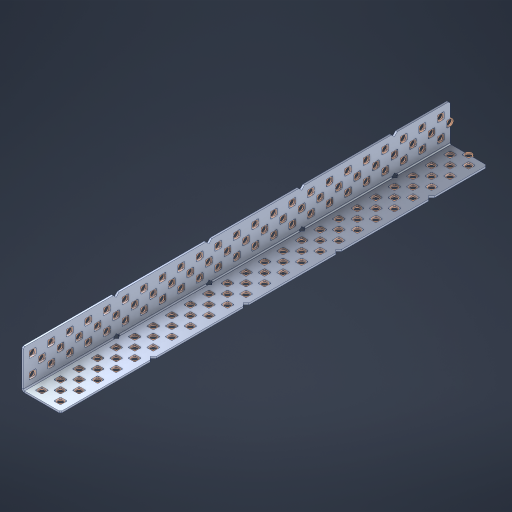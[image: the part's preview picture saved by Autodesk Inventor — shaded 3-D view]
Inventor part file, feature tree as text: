
AUTODESK INVENTOR PART (.ipt)
format: ipt  version: 2023 (Build 270158000, 158)  size: 1,684,992 bytes
history: native  units: in
note: dims shown in document units (in); Inventor stores cm internally (conversion verified against a paired STEP export)
features: other x144, extrude x136, sheet_metal_op x8, sketch x7, pattern_linear x2, mirror x1, chamfer x1
ambient origin geometry x8: Origin, YZ Plane, XZ Plane, XY Plane, X Axis, Y Axis, Z Axis, Center Point
bodies: Solid1 (feature_tree), Body (feature_tree)
feature tree (299):
  sheet_metal_op  "Flanges"
  sheet_metal_op  "Body Pattern"
  pattern_linear  "Center Pattern"  Spacing1=1.0in  [1 undecoded]
  other  "Arc Length"
  pattern_linear  "Notch Pattern"  Spacing1=0.1875in  [1 undecoded]
  other  "Diagonal Plane"
  mirror  "Everything Mirrored"
  chamfer  "End Chamfer"
  sketch  "Sketch1"  dims[d0=1.0in]
  other  "Plate1"
  sketch  "Sketch2"  dims[d1=11.5in]
  other  "Plate2"
  sheet_metal_op  "Bend1"
  sheet_metal_op  "Corner1"
  sketch  "Sketch8"  dims[d2=0.0469in]
  sketch  "Sketch9"  dims[d3=0.0469in]
  other  "Srf91"
  sheet_metal_op  "Body Pattern Sketch"
  other  "Srf92"
  sketch  "Sketch13"  dims[d4=0.0234in]
  sketch  "Sketch15"  dims[d5=0.0938in]
  sketch  "Sketch16"  dims[d6=0.0469in d7=1.0in d8=90.0deg d9=0.0312in d10=0.1875in d11=0.0469in d12=0.0469in d49=0.182in d50=0.02in d52=0.25in d53=0.0469in d54=0.0in d55=0.172in d56=1.0in d57=0.0in d60=9.0551in d62=0.5in d63=0.7874in d65=0.5in d85=0.1473in d86=0.1659in d89=0.0469in d90=0.0in d91=0.04in d92=0.0491in d95=2.5in d96=0.04in d97=0.25in d98=45.0deg d99=0.25in d106=0.182in d107=0.02in d108=0.5in d110=0.0469in d111=0.0in d112=0.172in d113=0.5in d114=0.0in d117=0.5in d123=0.25in d125=0.25in d126=0.0491in d127=0.1227in d128=0.08in d129=0.04in d130=2.5in]
  other  "Srf786"
  other  "Srf856"
  other  "Srf857"
  other  "Srf858"
  other  "Srf859"
  other  "Srf860"
  other  "Srf861"
  other  "Srf889"
  other  "Srf890"
  other  "Srf891"
  other  "Srf1275"
  other  "Srf1276"
  other  "Srf1278"
  other  "Srf1279"
  other  "Srf1280"
  other  "Srf1281"
  other  "Srf1282"
  other  "Srf1283"
  other  "Srf1277"
  other  "Srf1285"
  other  "Srf1286"
  other  "Srf1287"
  other  "Srf1383"
  other  "Srf1384"
  other  "Srf1385"
  other  "Srf1386"
  other  "Srf1387"
  other  "Srf1388"
  other  "Srf1389"
  other  "Srf1390"
  other  "Srf1391"
  other  "Srf1392"
  other  "Srf1393"
  other  "Srf1394"
  other  "Srf1395"
  other  "Srf1396"
  other  "Srf1397"
  other  "Srf1398"
  other  "Srf1399"
  other  "Srf1400"
  other  "Srf1401"
  other  "Srf1402"
  other  "Srf1403"
  other  "Srf1404"
  other  "Srf1405"
  other  "Srf1406"
  other  "Srf1407"
  other  "Srf1408"
  other  "Srf1409"
  other  "Srf1410"
  other  "Srf1411"
  other  "Srf1412"
  other  "Srf1413"
  other  "Srf1414"
  other  "Srf1415"
  other  "Srf1416"
  other  "Srf1417"
  other  "Srf1418"
  other  "Srf1419"
  other  "Srf1420"
  other  "Srf1445"
  other  "Srf1446"
  other  "Srf1447"
  other  "Srf1448"
  other  "Srf1449"
  other  "Srf1450"
  other  "Srf1451"
  other  "Srf1452"
  other  "Srf1453"
  other  "Srf1454"
  other  "Srf1455"
  other  "Srf1456"
  other  "Srf1457"
  other  "Srf1458"
  other  "Srf1459"
  other  "Srf1460"
  other  "Srf1461"
  other  "Srf1462"
  other  "Srf1463"
  other  "Srf1475"
  other  "Srf1476"
  other  "Srf1477"
  other  "Srf1478"
  other  "Srf1479"
  other  "Srf1480"
  other  "Srf1481"
  other  "Srf1482"
  other  "Srf1483"
  other  "Srf1484"
  other  "Srf1485"
  other  "Srf1486"
  other  "Srf1487"
  other  "Srf1488"
  other  "Srf1489"
  other  "Srf1490"
  other  "Srf1491"
  other  "Srf1492"
  other  "Srf1493"
  other  "Srf1494"
  other  "Srf1495"
  other  "Srf1496"
  other  "Srf1497"
  other  "Srf1498"
  other  "Srf1499"
  other  "Srf1500"
  other  "Srf1501"
  other  "Srf1502"
  other  "Srf1503"
  other  "Srf1504"
  other  "Srf1505"
  other  "Srf1506"
  other  "Srf1507"
  other  "Srf1508"
  other  "Srf1509"
  other  "Srf1510"
  other  "Srf1511"
  other  "Srf1512"
  other  "Srf1537"
  other  "Srf1538"
  other  "Srf1539"
  other  "Srf1540"
  other  "Srf1541"
  other  "Srf1542"
  other  "Srf1543"
  other  "Srf1544"
  other  "Srf1545"
  other  "Srf1546"
  other  "Srf1547"
  other  "Srf1548"
  other  "Srf1549"
  other  "Srf1550"
  other  "Srf1551"
  other  "Srf1552"
  other  "Srf1553"
  other  "Srf1554"
  other  "Srf1555"
  sheet_metal_op  "Body Stamp"
  sheet_metal_op  "Body Circle"
  other  "Center Stamp"
  other  "Center Circle"
  sheet_metal_op  "Notch"
  extrude  "ExtrusionSrf92"  Depth=0.0469in
  extrude  "ExtrusionSrf856"  Depth=0.0469in
  extrude  "ExtrusionSrf857"  Depth=0.182in
  extrude  "ExtrusionSrf858"  Depth=0.02in
  extrude  "ExtrusionSrf859"  Depth=0.25in
  extrude  "ExtrusionSrf860"  Depth=0.0469in
  extrude  "ExtrusionSrf861"  TaperAngle=0.0deg  [1 undecoded]
  extrude  "ExtrusionSrf889"  Depth=2.5in
  extrude  "ExtrusionSrf890"  Depth=1.0in TaperAngle=0.0deg
  extrude  "ExtrusionSrf891"  Depth=2.5in
  extrude  "ExtrusionSrf1275"  Depth=0.5in
  extrude  "ExtrusionSrf1276"  Depth=2.5in
  extrude  "ExtrusionSrf1277"  Depth=2.5in
  extrude  "ExtrusionSrf1278"  Depth=0.0469in
  extrude  "ExtrusionSrf1279"  Depth=2.5in TaperAngle=0.0deg
  extrude  "ExtrusionSrf1280"  Depth=2.5in
  extrude  "ExtrusionSrf1281"  Depth=0.25in TaperAngle=45.0deg
  extrude  "ExtrusionSrf1282"  Depth=0.25in
  extrude  "ExtrusionSrf1345"  Depth=0.182in
  extrude  "ExtrusionSrf1346"  Depth=0.02in
  extrude  "ExtrusionSrf1347"  Depth=0.5in
  extrude  "ExtrusionSrf1348"  Depth=0.0469in
  extrude  "ExtrusionSrf1383"  TaperAngle=0.0deg  [1 undecoded]
  extrude  "ExtrusionSrf1384"  Depth=2.5in
  extrude  "ExtrusionSrf1385"  Depth=0.5in TaperAngle=0.0deg
  extrude  "ExtrusionSrf1386"  Depth=0.5in
  extrude  "ExtrusionSrf1387"  Depth=0.25in
  extrude  "ExtrusionSrf1388"  Depth=0.25in
  extrude  "ExtrusionSrf1389"  Depth=2.5in
  extrude  "ExtrusionSrf1390"  Depth=2.5in
  extrude  "ExtrusionSrf1391"  Depth=2.5in
  extrude  "ExtrusionSrf1392"  Depth=2.5in
  extrude  "ExtrusionSrf1393"  Depth=2.5in
  extrude  "ExtrusionSrf1394"  [1 undecoded]
  extrude  "ExtrusionSrf1395"  [1 undecoded]
  extrude  "ExtrusionSrf1396"  [1 undecoded]
  extrude  "ExtrusionSrf1397"  [1 undecoded]
  extrude  "ExtrusionSrf1398"  [1 undecoded]
  extrude  "ExtrusionSrf1399"  [1 undecoded]
  extrude  "ExtrusionSrf1400"  [1 undecoded]
  extrude  "ExtrusionSrf1401"  [1 undecoded]
  extrude  "ExtrusionSrf1402"  [1 undecoded]
  extrude  "ExtrusionSrf1403"  [1 undecoded]
  extrude  "ExtrusionSrf1404"  [1 undecoded]
  extrude  "ExtrusionSrf1405"  [1 undecoded]
  extrude  "ExtrusionSrf1406"  [1 undecoded]
  extrude  "ExtrusionSrf1407"  [1 undecoded]
  extrude  "ExtrusionSrf1408"  [1 undecoded]
  extrude  "ExtrusionSrf1409"  [1 undecoded]
  extrude  "ExtrusionSrf1410"  [1 undecoded]
  extrude  "ExtrusionSrf1411"  [1 undecoded]
  extrude  "ExtrusionSrf1412"  [1 undecoded]
  extrude  "ExtrusionSrf1413"  [1 undecoded]
  extrude  "ExtrusionSrf1414"  [1 undecoded]
  extrude  "ExtrusionSrf1415"  [1 undecoded]
  extrude  "ExtrusionSrf1416"  [1 undecoded]
  extrude  "ExtrusionSrf1417"  [1 undecoded]
  extrude  "ExtrusionSrf1418"  [1 undecoded]
  extrude  "ExtrusionSrf1419"  [1 undecoded]
  extrude  "ExtrusionSrf1420"  [1 undecoded]
  extrude  "ExtrusionSrf1445"  [1 undecoded]
  extrude  "ExtrusionSrf1446"  [1 undecoded]
  extrude  "ExtrusionSrf1447"  [1 undecoded]
  extrude  "ExtrusionSrf1448"  [1 undecoded]
  extrude  "ExtrusionSrf1449"  [1 undecoded]
  extrude  "ExtrusionSrf1450"  [1 undecoded]
  extrude  "ExtrusionSrf1451"  [1 undecoded]
  extrude  "ExtrusionSrf1452"  [1 undecoded]
  extrude  "ExtrusionSrf1453"  [1 undecoded]
  extrude  "ExtrusionSrf1454"  [1 undecoded]
  extrude  "ExtrusionSrf1455"  [1 undecoded]
  extrude  "ExtrusionSrf1456"  [1 undecoded]
  extrude  "ExtrusionSrf1457"  [1 undecoded]
  extrude  "ExtrusionSrf1458"  [1 undecoded]
  extrude  "ExtrusionSrf1459"  [1 undecoded]
  extrude  "ExtrusionSrf1460"  [1 undecoded]
  extrude  "ExtrusionSrf1461"  [1 undecoded]
  extrude  "ExtrusionSrf1462"  [1 undecoded]
  extrude  "ExtrusionSrf1463"  [1 undecoded]
  extrude  "ExtrusionSrf1475"  [1 undecoded]
  extrude  "ExtrusionSrf1476"  [1 undecoded]
  extrude  "ExtrusionSrf1477"  [1 undecoded]
  extrude  "ExtrusionSrf1478"  [1 undecoded]
  extrude  "ExtrusionSrf1479"  [1 undecoded]
  extrude  "ExtrusionSrf1480"  [1 undecoded]
  extrude  "ExtrusionSrf1481"  [1 undecoded]
  extrude  "ExtrusionSrf1482"  [1 undecoded]
  extrude  "ExtrusionSrf1483"  [1 undecoded]
  extrude  "ExtrusionSrf1484"  [1 undecoded]
  extrude  "ExtrusionSrf1485"  [1 undecoded]
  extrude  "ExtrusionSrf1486"  [1 undecoded]
  extrude  "ExtrusionSrf1487"  [1 undecoded]
  extrude  "ExtrusionSrf1488"  [1 undecoded]
  extrude  "ExtrusionSrf1489"  [1 undecoded]
  extrude  "ExtrusionSrf1490"  [1 undecoded]
  extrude  "ExtrusionSrf1491"  [1 undecoded]
  extrude  "ExtrusionSrf1492"  [1 undecoded]
  extrude  "ExtrusionSrf1493"  [1 undecoded]
  extrude  "ExtrusionSrf1494"  [1 undecoded]
  extrude  "ExtrusionSrf1495"  [1 undecoded]
  extrude  "ExtrusionSrf1496"  [1 undecoded]
  extrude  "ExtrusionSrf1497"  [1 undecoded]
  extrude  "ExtrusionSrf1498"  [1 undecoded]
  extrude  "ExtrusionSrf1499"  [1 undecoded]
  extrude  "ExtrusionSrf1500"  [1 undecoded]
  extrude  "ExtrusionSrf1501"  [1 undecoded]
  extrude  "ExtrusionSrf1502"  [1 undecoded]
  extrude  "ExtrusionSrf1503"  [1 undecoded]
  extrude  "ExtrusionSrf1504"  [1 undecoded]
  extrude  "ExtrusionSrf1505"  [1 undecoded]
  extrude  "ExtrusionSrf1506"  [1 undecoded]
  extrude  "ExtrusionSrf1507"  [1 undecoded]
  extrude  "ExtrusionSrf1508"  [1 undecoded]
  extrude  "ExtrusionSrf1509"  [1 undecoded]
  extrude  "ExtrusionSrf1510"  [1 undecoded]
  extrude  "ExtrusionSrf1511"  [1 undecoded]
  extrude  "ExtrusionSrf1512"  [1 undecoded]
  extrude  "ExtrusionSrf1537"  [1 undecoded]
  extrude  "ExtrusionSrf1538"  [1 undecoded]
  extrude  "ExtrusionSrf1539"  [1 undecoded]
  extrude  "ExtrusionSrf1540"  [1 undecoded]
  extrude  "ExtrusionSrf1541"  [1 undecoded]
  extrude  "ExtrusionSrf1542"  [1 undecoded]
  extrude  "ExtrusionSrf1543"  [1 undecoded]
  extrude  "ExtrusionSrf1544"  [1 undecoded]
  extrude  "ExtrusionSrf1545"  [1 undecoded]
  extrude  "ExtrusionSrf1546"  [1 undecoded]
  extrude  "ExtrusionSrf1547"  [1 undecoded]
  extrude  "ExtrusionSrf1548"  [1 undecoded]
  extrude  "ExtrusionSrf1549"  [1 undecoded]
  extrude  "ExtrusionSrf1550"  [1 undecoded]
  extrude  "ExtrusionSrf1551"  [1 undecoded]
  extrude  "ExtrusionSrf1552"  [1 undecoded]
  extrude  "ExtrusionSrf1553"  [1 undecoded]
  extrude  "ExtrusionSrf1554"  [1 undecoded]
  extrude  "ExtrusionSrf1555"  [1 undecoded]
note: 107 required parameter values undecoded (feature->parameter linkage not recoverable at this tier; creation-order binding heuristic only, values carry confidence <= 0.55)
